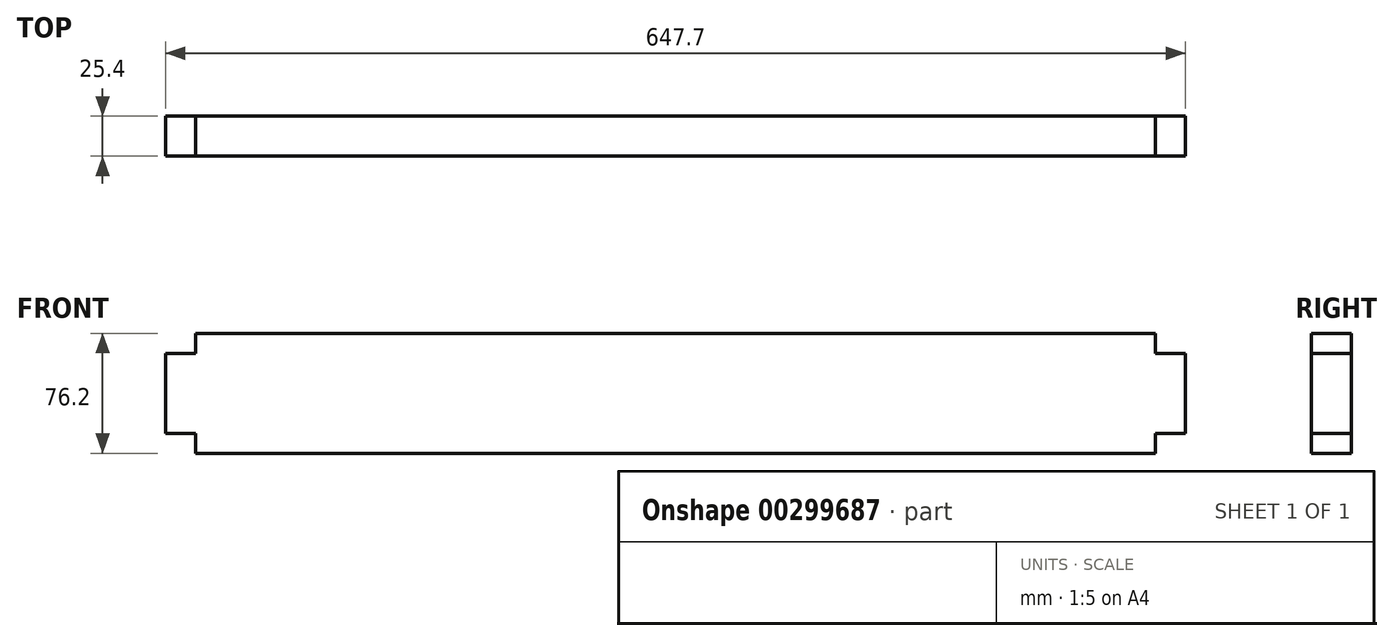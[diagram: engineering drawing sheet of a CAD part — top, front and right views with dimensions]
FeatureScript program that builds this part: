
annotation { "Feature Type Name" : "Feature", "Feature Type Description" : "" }
export const myFeature = defineFeature(function(context is Context, id is Id, definition is map)
    precondition{}
    {
        {
            var Q0;
            Q0=qCreatedBy(makeId("Front.planeOp"),FACE);
            var sketch = newSketch(context, id + "F0", { "sketchPlane" : qUnion([Q0])});
            skLineSegment(sketch, "E0.bottom", {"start": v(-128.95, 37.8) * mm, "end": v(480.65, 37.8) * mm});
            skLineSegment(sketch, "E0.top", {"start": v(-128.95, -38.4) * mm, "end": v(480.65, -38.4) * mm});
            skLineSegment(sketch, "E0.left", {"start": v(-128.95, 37.8) * mm, "end": v(-128.95, -38.4) * mm});
            skLineSegment(sketch, "E0.right", {"start": v(480.65, 37.8) * mm, "end": v(480.65, -38.4) * mm});
            skLineSegment(sketch, "E1.bottom", {"start": v(480.65, -25.7) * mm, "end": v(499.7, -25.7) * mm});
            skLineSegment(sketch, "E1.top", {"start": v(480.65, 25.1) * mm, "end": v(499.7, 25.1) * mm});
            skLineSegment(sketch, "E1.left", {"start": v(480.65, -25.7) * mm, "end": v(480.65, 25.1) * mm});
            skLineSegment(sketch, "E1.right", {"start": v(499.7, -25.7) * mm, "end": v(499.7, 25.1) * mm});
            skLineSegment(sketch, "E2.bottom", {"start": v(-128.95, 25.1) * mm, "end": v(-148, 25.1) * mm});
            skLineSegment(sketch, "E2.top", {"start": v(-128.95, -25.7) * mm, "end": v(-148, -25.7) * mm});
            skLineSegment(sketch, "E2.left", {"start": v(-128.95, 25.1) * mm, "end": v(-128.95, -25.7) * mm});
            skLineSegment(sketch, "E2.right", {"start": v(-148, 25.1) * mm, "end": v(-148, -25.7) * mm});
            skSolve(sketch);
        }
        {
            var Q0;
            Q0 = qSketchRegion(id + "F0", true);
            extrude(context, id + "F1", {"entities" : qUnion([Q0]), "depth" : 25.4 * mm});
        }
    });
